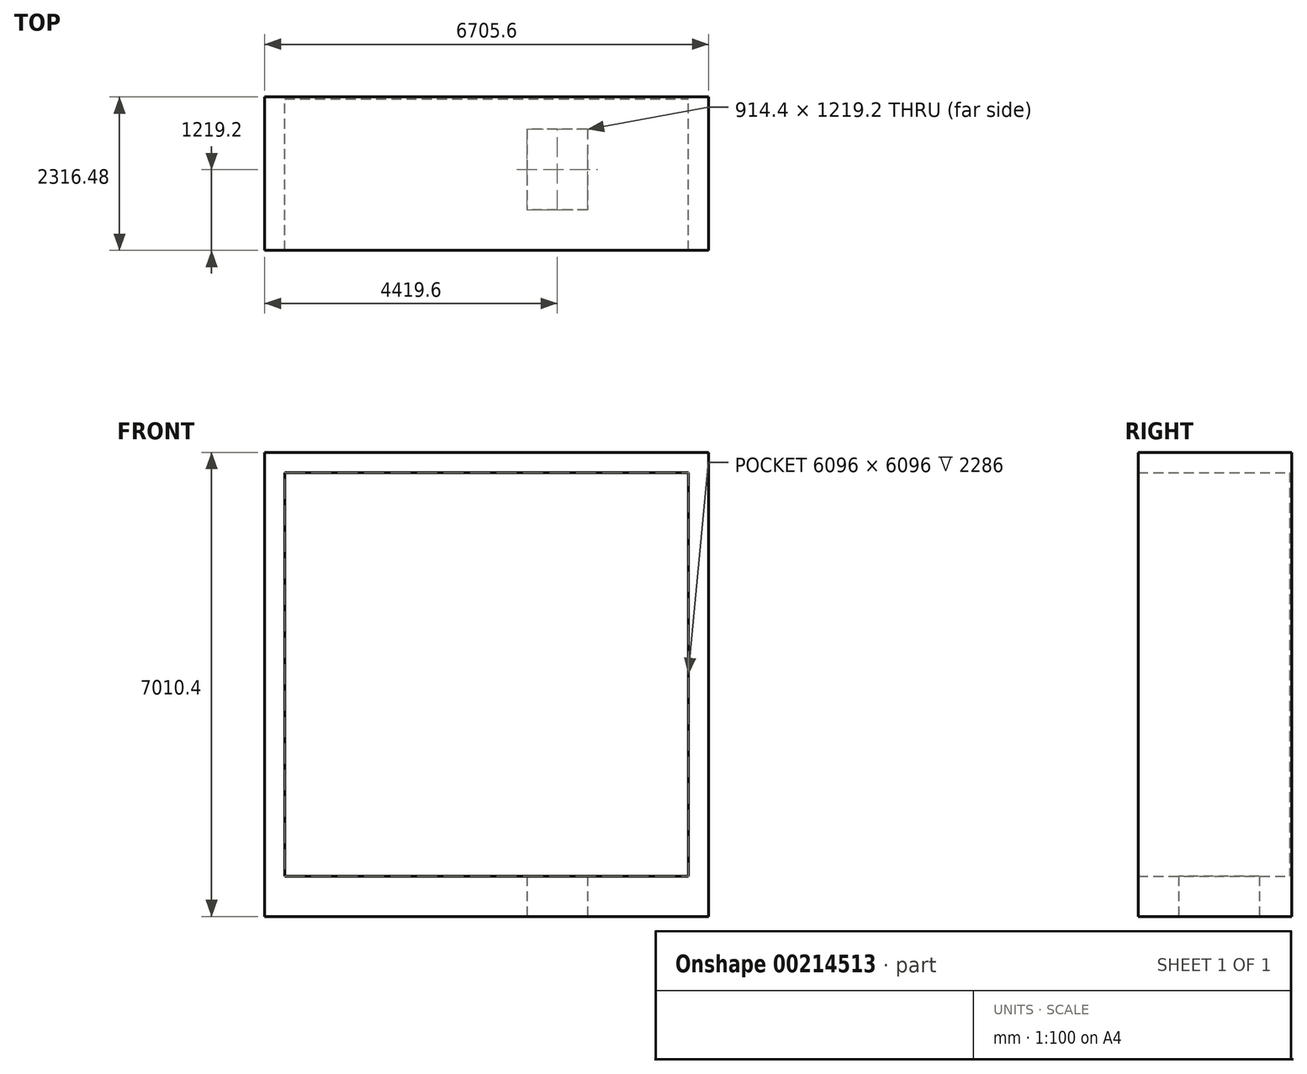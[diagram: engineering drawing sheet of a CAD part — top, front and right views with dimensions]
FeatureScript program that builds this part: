
annotation { "Feature Type Name" : "Feature", "Feature Type Description" : "" }
export const myFeature = defineFeature(function(context is Context, id is Id, definition is map)
    precondition{}
    {
        {
            var Q0;
            Q0=qCreatedBy(makeId("Front.planeOp"),FACE);
            var sketch = newSketch(context, id + "F0", { "sketchPlane" : qUnion([Q0])});
            skLineSegment(sketch, "E0.bottom", {"start": v(-3048, 3048) * mm, "end": v(3048, 3048) * mm});
            skLineSegment(sketch, "E0.top", {"start": v(-3048, -3048) * mm, "end": v(3048, -3048) * mm});
            skLineSegment(sketch, "E0.left", {"start": v(-3048, 3048) * mm, "end": v(-3048, -3048) * mm});
            skLineSegment(sketch, "E0.right", {"start": v(3048, 3048) * mm, "end": v(3048, -3048) * mm});
            skPoint(sketch, "E0.middle", {"position": v(0, 0) * mm});
            skLineSegment(sketch, "E1.0", {"start": v(-3352.8, 3352.8) * mm, "end": v(3352.8, 3352.8) * mm});
            skLineSegment(sketch, "E2.0", {"start": v(-3352.8, -3657.6) * mm, "end": v(3352.8, -3657.6) * mm});
            skLineSegment(sketch, "E3.0", {"start": v(-3352.8, 3352.8) * mm, "end": v(-3352.8, -3657.6) * mm});
            skLineSegment(sketch, "E4.0", {"start": v(3352.8, 3352.8) * mm, "end": v(3352.8, -3657.6) * mm});
            skSolve(sketch);
        }
        {
            var Q0;
            Q0=makeQuery(id+"F0.imprint","IMPRINT",FACE,{"disambiguationData":[TD([[makeQuery(id+"F0.imprint","IMPRINT",EDGE,{"derivedFrom":sQuery(id+"F0.wireOp",EDGE,"E0.bottom")}),1.0]])]});
            extrude(context, id + "F1", {"entities" : qUnion([Q0]), "depth" : 2316.48 * mm});
        }
        {
            var Q0;
            Q0=makeQuery(id+"F0.imprint","IMPRINT",FACE,{"disambiguationData":[TD([[makeQuery(id+"F0.imprint","IMPRINT",EDGE,{"derivedFrom":sQuery(id+"F0.wireOp",EDGE,"E0.bottom")}),-1.0]])]});
            extrude(context, id + "F2", {"entities" : qUnion([Q0]), "operationType" : NewBodyOperationType.ADD, "depth" : 30.48 * mm});
        }
        {
            var Q0;
            Q0=makeQuery(id+"F2.opExtrude","CAP_FACE",FACE,{"disambiguationData":[OSD([sQuery(id+"F0.wireOp",EDGE,"E0.bottom"),sQuery(id+"F0.wireOp",EDGE,"E0.top"),sQuery(id+"F0.wireOp",EDGE,"E0.left"),sQuery(id+"F0.wireOp",EDGE,"E0.right")])],"isStart":false});
            var sketch = newSketch(context, id + "F3", { "sketchPlane" : qUnion([Q0])});
            skLineSegment(sketch, "E5.0.0", {"start": v(-3048, 3048) * mm, "end": v(-3048, -3048) * mm, "construction": true});
            skLineSegment(sketch, "E5.0.1", {"start": v(-3048, -3048) * mm, "end": v(3048, -3048) * mm, "construction": true});
            skLineSegment(sketch, "E5.0.2", {"start": v(3048, -3048) * mm, "end": v(3048, 3048) * mm, "construction": true});
            skLineSegment(sketch, "E5.0.3", {"start": v(3048, 3048) * mm, "end": v(-3048, 3048) * mm, "construction": true});
            skLineSegment(sketch, "E6", {"start": v(-3048, -2438.4) * mm, "end": v(-2438.4, -2438.4) * mm, "construction": true});
            skLineSegment(sketch, "E7", {"start": v(-2438.4, -2438.4) * mm, "end": v(-2438.4, -3048) * mm, "construction": true});
            skCircle(sketch, "E8", {"center": v(-2438.4, -2438.4) * mm, "radius": 304.8 * mm});
            skCircle(sketch, "E9.0.1.0", {"center": v(-2438.4, -1463.04) * mm, "radius": 304.8 * mm});
            skCircle(sketch, "E9.0.2.0", {"center": v(-2438.4, -487.68) * mm, "radius": 304.8 * mm});
            skCircle(sketch, "E9.0.3.0", {"center": v(-2438.4, 487.68) * mm, "radius": 304.8 * mm});
            skCircle(sketch, "E9.0.4.0", {"center": v(-2438.4, 1463.04) * mm, "radius": 304.8 * mm});
            skCircle(sketch, "E9.0.5.0", {"center": v(-2438.4, 2438.4) * mm, "radius": 304.8 * mm});
            skCircle(sketch, "E9.1.0.0", {"center": v(-1219.2, -2438.4) * mm, "radius": 304.8 * mm});
            skCircle(sketch, "E9.1.1.0", {"center": v(-1219.2, -1463.04) * mm, "radius": 304.8 * mm});
            skCircle(sketch, "E9.1.2.0", {"center": v(-1219.2, -487.68) * mm, "radius": 304.8 * mm});
            skCircle(sketch, "E9.1.3.0", {"center": v(-1219.2, 487.68) * mm, "radius": 304.8 * mm});
            skCircle(sketch, "E9.1.4.0", {"center": v(-1219.2, 1463.04) * mm, "radius": 304.8 * mm});
            skCircle(sketch, "E9.1.5.0", {"center": v(-1219.2, 2438.4) * mm, "radius": 304.8 * mm});
            skCircle(sketch, "E9.2.0.0", {"center": v(0, -2438.4) * mm, "radius": 304.8 * mm});
            skCircle(sketch, "E9.2.1.0", {"center": v(0, -1463.04) * mm, "radius": 304.8 * mm});
            skCircle(sketch, "E9.2.2.0", {"center": v(0, -487.68) * mm, "radius": 304.8 * mm});
            skCircle(sketch, "E9.2.3.0", {"center": v(0, 487.68) * mm, "radius": 304.8 * mm});
            skCircle(sketch, "E9.2.4.0", {"center": v(0, 1463.04) * mm, "radius": 304.8 * mm});
            skCircle(sketch, "E9.2.5.0", {"center": v(0, 2438.4) * mm, "radius": 304.8 * mm});
            skCircle(sketch, "E9.3.0.0", {"center": v(1219.2, -2438.4) * mm, "radius": 304.8 * mm});
            skCircle(sketch, "E9.3.1.0", {"center": v(1219.2, -1463.04) * mm, "radius": 304.8 * mm});
            skCircle(sketch, "E9.3.2.0", {"center": v(1219.2, -487.68) * mm, "radius": 304.8 * mm});
            skCircle(sketch, "E9.3.3.0", {"center": v(1219.2, 487.68) * mm, "radius": 304.8 * mm});
            skCircle(sketch, "E9.3.4.0", {"center": v(1219.2, 1463.04) * mm, "radius": 304.8 * mm});
            skCircle(sketch, "E9.3.5.0", {"center": v(1219.2, 2438.4) * mm, "radius": 304.8 * mm});
            skCircle(sketch, "E9.4.0.0", {"center": v(2438.4, -2438.4) * mm, "radius": 304.8 * mm});
            skCircle(sketch, "E9.4.1.0", {"center": v(2438.4, -1463.04) * mm, "radius": 304.8 * mm});
            skCircle(sketch, "E9.4.2.0", {"center": v(2438.4, -487.68) * mm, "radius": 304.8 * mm});
            skCircle(sketch, "E9.4.3.0", {"center": v(2438.4, 487.68) * mm, "radius": 304.8 * mm});
            skCircle(sketch, "E9.4.4.0", {"center": v(2438.4, 1463.04) * mm, "radius": 304.8 * mm});
            skCircle(sketch, "E9.4.5.0", {"center": v(2438.4, 2438.4) * mm, "radius": 304.8 * mm});
            skLineSegment(sketch, "E9.direction1", {"start": v(-2438.4, -2438.4) * mm, "end": v(-1219.2, -2438.4) * mm, "construction": true});
            skLineSegment(sketch, "E9.direction2", {"start": v(-2438.4, -2438.4) * mm, "end": v(-2438.4, -1463.04) * mm, "construction": true});
            skSolve(sketch);
        }
        {
            var Q0;
            Q0=makeQuery(id+"F3.imprint","IMPRINT",FACE,{"disambiguationData":[TD([[makeQuery(id+"F3.imprint","IMPRINT",EDGE,{"derivedFrom":sQuery(id+"F3.wireOp",EDGE,"E9.0.5.0")}),1.0]])]});
            var Q1;
            Q1=makeQuery(id+"F3.imprint","IMPRINT",FACE,{"disambiguationData":[TD([[makeQuery(id+"F3.imprint","IMPRINT",EDGE,{"derivedFrom":sQuery(id+"F3.wireOp",EDGE,"E9.1.5.0")}),1.0]])]});
            var Q2;
            Q2=makeQuery(id+"F3.imprint","IMPRINT",FACE,{"disambiguationData":[TD([[makeQuery(id+"F3.imprint","IMPRINT",EDGE,{"derivedFrom":sQuery(id+"F3.wireOp",EDGE,"E9.2.5.0")}),1.0]])]});
            var Q3;
            Q3=makeQuery(id+"F3.imprint","IMPRINT",FACE,{"disambiguationData":[TD([[makeQuery(id+"F3.imprint","IMPRINT",EDGE,{"derivedFrom":sQuery(id+"F3.wireOp",EDGE,"E9.3.5.0")}),1.0]])]});
            var Q4;
            Q4=makeQuery(id+"F3.imprint","IMPRINT",FACE,{"disambiguationData":[TD([[makeQuery(id+"F3.imprint","IMPRINT",EDGE,{"derivedFrom":sQuery(id+"F3.wireOp",EDGE,"E9.4.5.0")}),1.0]])]});
            var Q5;
            Q5=makeQuery(id+"F3.imprint","IMPRINT",FACE,{"disambiguationData":[TD([[makeQuery(id+"F3.imprint","IMPRINT",EDGE,{"derivedFrom":sQuery(id+"F3.wireOp",EDGE,"E9.4.4.0")}),1.0]])]});
            var Q6;
            Q6=makeQuery(id+"F3.imprint","IMPRINT",FACE,{"disambiguationData":[TD([[makeQuery(id+"F3.imprint","IMPRINT",EDGE,{"derivedFrom":sQuery(id+"F3.wireOp",EDGE,"E9.3.4.0")}),1.0]])]});
            var Q7;
            Q7=makeQuery(id+"F3.imprint","IMPRINT",FACE,{"disambiguationData":[TD([[makeQuery(id+"F3.imprint","IMPRINT",EDGE,{"derivedFrom":sQuery(id+"F3.wireOp",EDGE,"E9.1.4.0")}),1.0]])]});
            var Q8;
            Q8=makeQuery(id+"F3.imprint","IMPRINT",FACE,{"disambiguationData":[TD([[makeQuery(id+"F3.imprint","IMPRINT",EDGE,{"derivedFrom":sQuery(id+"F3.wireOp",EDGE,"E9.2.4.0")}),1.0]])]});
            var Q9;
            Q9=makeQuery(id+"F3.imprint","IMPRINT",FACE,{"disambiguationData":[TD([[makeQuery(id+"F3.imprint","IMPRINT",EDGE,{"derivedFrom":sQuery(id+"F3.wireOp",EDGE,"E9.0.4.0")}),1.0]])]});
            var Q10;
            Q10=makeQuery(id+"F3.imprint","IMPRINT",FACE,{"disambiguationData":[TD([[makeQuery(id+"F3.imprint","IMPRINT",EDGE,{"derivedFrom":sQuery(id+"F3.wireOp",EDGE,"E9.0.2.0")}),1.0]])]});
            var Q11;
            Q11=makeQuery(id+"F3.imprint","IMPRINT",FACE,{"disambiguationData":[TD([[makeQuery(id+"F3.imprint","IMPRINT",EDGE,{"derivedFrom":sQuery(id+"F3.wireOp",EDGE,"E9.0.3.0")}),1.0]])]});
            var Q12;
            Q12=makeQuery(id+"F3.imprint","IMPRINT",FACE,{"disambiguationData":[TD([[makeQuery(id+"F3.imprint","IMPRINT",EDGE,{"derivedFrom":sQuery(id+"F3.wireOp",EDGE,"E9.1.3.0")}),1.0]])]});
            var Q13;
            Q13=makeQuery(id+"F3.imprint","IMPRINT",FACE,{"disambiguationData":[TD([[makeQuery(id+"F3.imprint","IMPRINT",EDGE,{"derivedFrom":sQuery(id+"F3.wireOp",EDGE,"E9.2.3.0")}),1.0]])]});
            var Q14;
            Q14=makeQuery(id+"F3.imprint","IMPRINT",FACE,{"disambiguationData":[TD([[makeQuery(id+"F3.imprint","IMPRINT",EDGE,{"derivedFrom":sQuery(id+"F3.wireOp",EDGE,"E9.3.3.0")}),1.0]])]});
            var Q15;
            Q15=makeQuery(id+"F3.imprint","IMPRINT",FACE,{"disambiguationData":[TD([[makeQuery(id+"F3.imprint","IMPRINT",EDGE,{"derivedFrom":sQuery(id+"F3.wireOp",EDGE,"E9.4.3.0")}),1.0]])]});
            var Q16;
            Q16=makeQuery(id+"F3.imprint","IMPRINT",FACE,{"disambiguationData":[TD([[makeQuery(id+"F3.imprint","IMPRINT",EDGE,{"derivedFrom":sQuery(id+"F3.wireOp",EDGE,"E9.4.2.0")}),1.0]])]});
            var Q17;
            Q17=makeQuery(id+"F3.imprint","IMPRINT",FACE,{"disambiguationData":[TD([[makeQuery(id+"F3.imprint","IMPRINT",EDGE,{"derivedFrom":sQuery(id+"F3.wireOp",EDGE,"E9.3.2.0")}),1.0]])]});
            var Q18;
            Q18=makeQuery(id+"F3.imprint","IMPRINT",FACE,{"disambiguationData":[TD([[makeQuery(id+"F3.imprint","IMPRINT",EDGE,{"derivedFrom":sQuery(id+"F3.wireOp",EDGE,"E9.2.2.0")}),1.0]])]});
            var Q19;
            Q19=makeQuery(id+"F3.imprint","IMPRINT",FACE,{"disambiguationData":[TD([[makeQuery(id+"F3.imprint","IMPRINT",EDGE,{"derivedFrom":sQuery(id+"F3.wireOp",EDGE,"E9.1.2.0")}),1.0]])]});
            var Q20;
            Q20=makeQuery(id+"F3.imprint","IMPRINT",FACE,{"disambiguationData":[TD([[makeQuery(id+"F3.imprint","IMPRINT",EDGE,{"derivedFrom":sQuery(id+"F3.wireOp",EDGE,"E9.1.1.0")}),1.0]])]});
            var Q21;
            Q21=makeQuery(id+"F3.imprint","IMPRINT",FACE,{"disambiguationData":[TD([[makeQuery(id+"F3.imprint","IMPRINT",EDGE,{"derivedFrom":sQuery(id+"F3.wireOp",EDGE,"E9.0.1.0")}),1.0]])]});
            var Q22;
            Q22=makeQuery(id+"F3.imprint","IMPRINT",FACE,{"disambiguationData":[TD([[makeQuery(id+"F3.imprint","IMPRINT",EDGE,{"derivedFrom":sQuery(id+"F3.wireOp",EDGE,"E8")}),1.0]])]});
            var Q23;
            Q23=makeQuery(id+"F3.imprint","IMPRINT",FACE,{"disambiguationData":[TD([[makeQuery(id+"F3.imprint","IMPRINT",EDGE,{"derivedFrom":sQuery(id+"F3.wireOp",EDGE,"E9.1.0.0")}),1.0]])]});
            var Q24;
            Q24=makeQuery(id+"F3.imprint","IMPRINT",FACE,{"disambiguationData":[TD([[makeQuery(id+"F3.imprint","IMPRINT",EDGE,{"derivedFrom":sQuery(id+"F3.wireOp",EDGE,"E9.2.0.0")}),1.0]])]});
            var Q25;
            Q25=makeQuery(id+"F3.imprint","IMPRINT",FACE,{"disambiguationData":[TD([[makeQuery(id+"F3.imprint","IMPRINT",EDGE,{"derivedFrom":sQuery(id+"F3.wireOp",EDGE,"E9.3.0.0")}),1.0]])]});
            var Q26;
            Q26=makeQuery(id+"F3.imprint","IMPRINT",FACE,{"disambiguationData":[TD([[makeQuery(id+"F3.imprint","IMPRINT",EDGE,{"derivedFrom":sQuery(id+"F3.wireOp",EDGE,"E9.4.0.0")}),1.0]])]});
            var Q27;
            Q27=makeQuery(id+"F3.imprint","IMPRINT",FACE,{"disambiguationData":[TD([[makeQuery(id+"F3.imprint","IMPRINT",EDGE,{"derivedFrom":sQuery(id+"F3.wireOp",EDGE,"E9.4.1.0")}),1.0]])]});
            var Q28;
            Q28=makeQuery(id+"F3.imprint","IMPRINT",FACE,{"disambiguationData":[TD([[makeQuery(id+"F3.imprint","IMPRINT",EDGE,{"derivedFrom":sQuery(id+"F3.wireOp",EDGE,"E9.3.1.0")}),1.0]])]});
            var Q29;
            Q29=makeQuery(id+"F3.imprint","IMPRINT",FACE,{"disambiguationData":[TD([[makeQuery(id+"F3.imprint","IMPRINT",EDGE,{"derivedFrom":sQuery(id+"F3.wireOp",EDGE,"E9.2.1.0")}),1.0]])]});
            var Q30;
            Q30=sQuery(id+"F3.wireOp",EDGE,"E9.0.5.0");
            var Q31;
            Q31=sQuery(id+"F3.wireOp",EDGE,"E9.0.4.0");
            var Q32;
            Q32=sQuery(id+"F3.wireOp",EDGE,"E9.0.3.0");
            var Q33;
            Q33=sQuery(id+"F3.wireOp",EDGE,"E9.0.2.0");
            var Q34;
            Q34=sQuery(id+"F3.wireOp",EDGE,"E9.1.2.0");
            var Q35;
            Q35=sQuery(id+"F3.wireOp",EDGE,"E9.0.1.0");
            var Q36;
            Q36=sQuery(id+"F3.wireOp",EDGE,"E8");
            var Q37;
            Q37=sQuery(id+"F3.wireOp",EDGE,"E9.1.3.0");
            var Q38;
            Q38=sQuery(id+"F3.wireOp",EDGE,"E9.2.3.0");
            var Q39;
            Q39=sQuery(id+"F3.wireOp",EDGE,"E9.2.2.0");
            var Q40;
            Q40=sQuery(id+"F3.wireOp",EDGE,"E9.1.1.0");
            var Q41;
            Q41=sQuery(id+"F3.wireOp",EDGE,"E9.1.0.0");
            var Q42;
            Q42=sQuery(id+"F3.wireOp",EDGE,"E9.2.0.0");
            var Q43;
            Q43=sQuery(id+"F3.wireOp",EDGE,"E9.3.0.0");
            var Q44;
            Q44=sQuery(id+"F3.wireOp",EDGE,"E9.2.1.0");
            var Q45;
            Q45=sQuery(id+"F3.wireOp",EDGE,"E9.3.1.0");
            var Q46;
            Q46=sQuery(id+"F3.wireOp",EDGE,"E9.4.1.0");
            var Q47;
            Q47=sQuery(id+"F3.wireOp",EDGE,"E9.4.0.0");
            var Q48;
            Q48=sQuery(id+"F3.wireOp",EDGE,"E9.4.2.0");
            var Q49;
            Q49=sQuery(id+"F3.wireOp",EDGE,"E9.3.2.0");
            var Q50;
            Q50=sQuery(id+"F3.wireOp",EDGE,"E9.3.3.0");
            var Q51;
            Q51=sQuery(id+"F3.wireOp",EDGE,"E9.4.4.0");
            var Q52;
            Q52=sQuery(id+"F3.wireOp",EDGE,"E9.3.4.0");
            var Q53;
            Q53=sQuery(id+"F3.wireOp",EDGE,"E9.4.3.0");
            var Q54;
            Q54=sQuery(id+"F3.wireOp",EDGE,"E9.2.4.0");
            var Q55;
            Q55=sQuery(id+"F3.wireOp",EDGE,"E9.4.5.0");
            var Q56;
            Q56=sQuery(id+"F3.wireOp",EDGE,"E9.3.5.0");
            var Q57;
            Q57=sQuery(id+"F3.wireOp",EDGE,"E9.2.5.0");
            var Q58;
            Q58=sQuery(id+"F3.wireOp",EDGE,"E9.1.5.0");
            var Q59;
            Q59=sQuery(id+"F3.wireOp",EDGE,"E9.1.4.0");
            extrude(context, id + "F4", {"entities" : qUnion([Q0, Q1, Q2, Q3, Q4, Q5, Q6, Q7, Q8, Q9, Q10, Q11, Q12, Q13, Q14, Q15, Q16, Q17, Q18, Q19, Q20, Q21, Q22, Q23, Q24, Q25, Q26, Q27, Q28, Q29]), "bodyType" : ToolBodyType.SURFACE, "surfaceEntities" : qUnion([Q30, Q31, Q32, Q33, Q34, Q35, Q36, Q37, Q38, Q39, Q40, Q41, Q42, Q43, Q44, Q45, Q46, Q47, Q48, Q49, Q50, Q51, Q52, Q53, Q54, Q55, Q56, Q57, Q58, Q59]), "depth" : 914.4 * mm});
        }
        {
            var Q0;
            Q0=makeQuery(id+"F1.opExtrude","SWEPT_FACE",FACE,{"disambiguationData":[OSD([sQuery(id+"F0.wireOp",EDGE,"E2.0")])]});
            var sketch = newSketch(context, id + "F5", { "sketchPlane" : qUnion([Q0])});
            skLineSegment(sketch, "E10", {"start": v(3352.8, 1706.88) * mm, "end": v(1524, 1706.88) * mm, "construction": true});
            skLineSegment(sketch, "E11", {"start": v(1524, 1706.88) * mm, "end": v(1524, 2316.48) * mm, "construction": true});
            skLineSegment(sketch, "E12.bottom", {"start": v(1524, 487.68) * mm, "end": v(609.6, 487.68) * mm});
            skLineSegment(sketch, "E12.top", {"start": v(1524, 1706.88) * mm, "end": v(609.6, 1706.88) * mm});
            skLineSegment(sketch, "E12.left", {"start": v(1524, 487.68) * mm, "end": v(1524, 1706.88) * mm});
            skLineSegment(sketch, "E12.right", {"start": v(609.6, 487.68) * mm, "end": v(609.6, 1706.88) * mm});
            skPoint(sketch, "E12.middle", {"position": v(1066.8, 1097.28) * mm});
            skSolve(sketch);
        }
        {
            var Q0;
            Q0=makeQuery(id+"F5.imprint","IMPRINT",FACE,{"disambiguationData":[TD([[makeQuery(id+"F5.imprint","IMPRINT",EDGE,{"derivedFrom":sQuery(id+"F5.wireOp",EDGE,"E12.bottom")}),-1.0]])]});
            var Q1;
            Q1=makeQuery(id+"F1.opExtrude","SWEPT_FACE",FACE,{"disambiguationData":[OSD([sQuery(id+"F0.wireOp",EDGE,"E0.top")])]});
            extrude(context, id + "F6", {"entities" : qUnion([Q0]), "operationType" : NewBodyOperationType.REMOVE, "endBound" : BoundingType.UP_TO_SURFACE, "oppositeDirection" : true, "endBoundEntityFace" : qUnion([Q1]), "depth" : 30.48 * mm});
        }
        {
            var Q0;
            Q0=makeQuery(id+"F1.opExtrude","SWEPT_FACE",FACE,{"disambiguationData":[OSD([sQuery(id+"F0.wireOp",EDGE,"E0.bottom")])]});
            var sketch = newSketch(context, id + "F7", { "sketchPlane" : qUnion([Q0])});
            skLineSegment(sketch, "E13.0", {"start": v(-3352.8, 2316.48) * mm, "end": v(3352.8, 2316.48) * mm, "construction": true});
            skLineSegment(sketch, "E14.0", {"start": v(3352.8, 2316.48) * mm, "end": v(3352.8, 0) * mm, "construction": true});
            skLineSegment(sketch, "E15.0", {"start": v(-3352.8, 0) * mm, "end": v(3352.8, 0) * mm, "construction": true});
            skCircle(sketch, "E16", {"center": v(2895.6, 609.6) * mm, "radius": 76.2 * mm});
            skLineSegment(sketch, "E17", {"start": v(2895.6, 609.6) * mm, "end": v(3352.8, 609.6) * mm, "construction": true});
            skLineSegment(sketch, "E18", {"start": v(2895.6, 609.6) * mm, "end": v(2895.6, 0) * mm, "construction": true});
            skSolve(sketch);
        }
        {
            var Q0;
            Q0=makeQuery(id+"F7.imprint","IMPRINT",FACE,{"disambiguationData":[TD([[makeQuery(id+"F7.imprint","IMPRINT",EDGE,{"derivedFrom":sQuery(id+"F7.wireOp",EDGE,"E16")}),1.0]])]});
            var Q1;
            Q1=sQuery(id+"F7.wireOp",EDGE,"E16");
            extrude(context, id + "F8", {"entities" : qUnion([Q0]), "bodyType" : ToolBodyType.SURFACE, "surfaceEntities" : qUnion([Q1]), "depth" : 152.4 * mm});
        }
    });
